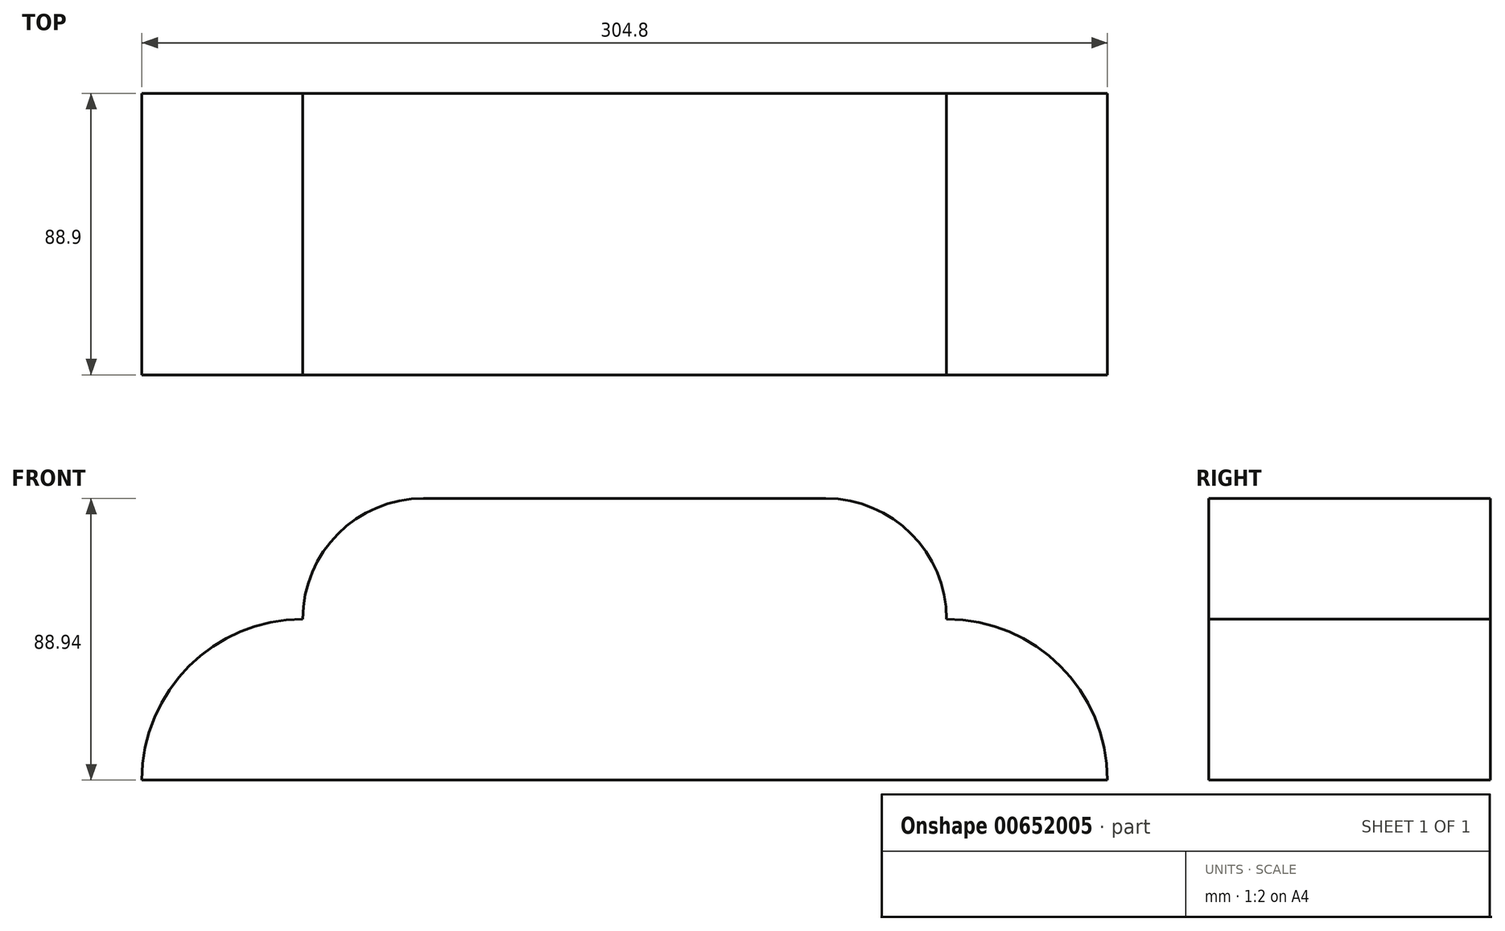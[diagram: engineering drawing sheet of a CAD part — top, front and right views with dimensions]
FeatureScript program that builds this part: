
annotation { "Feature Type Name" : "Feature", "Feature Type Description" : "" }
export const myFeature = defineFeature(function(context is Context, id is Id, definition is map)
    precondition{}
    {
        {
            var Q0;
            Q0=qCreatedBy(makeId("Front.planeOp"),FACE);
            var sketch = newSketch(context, id + "F0", { "sketchPlane" : qUnion([Q0])});
            skLineSegment(sketch, "E0.bottom", {"start": v(152.4, -44.47) * mm, "end": v(-152.4, -44.47) * mm});
            skLineSegment(sketch, "E0.top", {"start": v(63.5, 44.47) * mm, "end": v(-63.5, 44.47) * mm});
            skLineSegment(sketch, "E0.left", {"start": v(152.4, -44.47) * mm, "end": v(152.4, -44.43) * mm});
            skLineSegment(sketch, "E0.right", {"start": v(-152.4, -44.47) * mm, "end": v(-152.4, -44.43) * mm});
            skPoint(sketch, "E0.middle", {"position": v(0, 0) * mm});
            skPoint(sketch, "E1.newPointA", {"position": v(-152.4, 44.47) * mm});
            skArc(sketch, "E1.filletArc", {"start": v(-63.5, 44.47) * mm, "mid": v(-90.44, 33.3) * mm, "end": v(-101.6, 6.37) * mm});
            skPoint(sketch, "E2.newPointB", {"position": v(-152.4, 44.43) * mm});
            skArc(sketch, "E2.filletArc", {"start": v(-101.6, 6.37) * mm, "mid": v(-137.52, -8.51) * mm, "end": v(-152.4, -44.43) * mm});
            skArc(sketch, "E3.MirrorCS", {"start": v(63.5, 44.47) * mm, "mid": v(90.44, 33.3) * mm, "end": v(101.6, 6.37) * mm});
            skArc(sketch, "E4.MirrorCS", {"start": v(101.6, 6.37) * mm, "mid": v(137.52, -8.51) * mm, "end": v(152.4, -44.43) * mm});
            skPoint(sketch, "E5.orphan", {"position": v(152.4, 44.47) * mm});
            skSolve(sketch);
        }
        {
            var Q0;
            Q0=makeQuery(id+"F0.imprint","IMPRINT",FACE,{"disambiguationData":[TD([[makeQuery(id+"F0.imprint","IMPRINT",EDGE,{"derivedFrom":sQuery(id+"F0.wireOp",EDGE,"E0.bottom")}),-1.0]])]});
            extrude(context, id + "F1", {"entities" : qUnion([Q0]), "depth" : 88.9 * mm, "offsetDistance" : 25.4 * mm});
        }
    });
